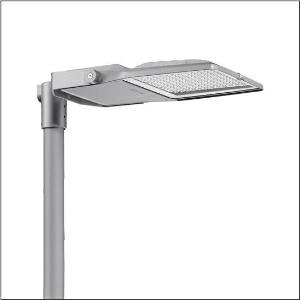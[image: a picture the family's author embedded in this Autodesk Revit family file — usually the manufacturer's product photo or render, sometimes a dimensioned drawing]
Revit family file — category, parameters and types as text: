
# Revit family: floodlight_fl_21_iq_midi___pl43_5xa7782f4a3a_c232
name_source: partatom
category: Lighting Fixtures
units: mm (PartAtom-declared; Revit-internal decimal feet)

## family parameters
Cut with Voids When Loaded = No
Host = Face
Light Source = No
Part Type = Normal
Room Calculation Point = No
Round Connector Dimension = Use Diameter
Shared = No

## types (1)
- --- (1 x LED, 38290 lm, 270.2 W, 4000K)
    Apparent Load = 270 VA
    CIE Flux Codes = 27 78 99 100 100
    Color Rendering = 70
    Color Temperature = 4000K
    Default Elevation = 1800 mm
    Description = Floodlight FL 21 iQ midi, floodlight, primary light control with lens, of PMMA, primary optical cover: protective disc, of toughened safety glass, transparent, light distribution: PL43, light emission: direct distribution, installation type: surface-mounted, lamps: LED, High Power LED, rated values: 38.290lm | 270,2W | 141,7lm/W (begin service life); end service life: 38.290lm | 286,6W; at 50% lumin. flux: 19.145lm | 117,7W | 162,7lm/W, colour temperature: 4000K, colour rendering: CRI > 70, light colour: 740, light setting 1 begin service life: 100% | 38.290lm | 270,2W | 141,7lm/W | 4.000K, light setting 1 end service life: 286,6W, further light settings possible, control: optimised constant luminous flux control (CLO 2.0), Desk-Remote (wireless, voltage-free reading and setting of iQ features in the workshop via application-optimized NFC function/RFID function), Smart-Wire, Night-Set, Temp-Guard, Auto-Match, Street-Remote, pre-setting: linear dimming characteristic, with terminal, 6-pole, mains connection: 220..240V, AC, 50/60Hz, luminaire housing, of diecast aluminium, powder-coated, SITECO metallic grey (DB 702S), corrosivity category C5 mid according to DIN EN ISO 12944suitable for swimming poolschlorine-resistant, sealing non-destructively replaceable, please order mast flange separately, mast bracket, of steel, galvanised, powder-coated, SITECO metallic grey (DB 702S), protection rating (complete): IP66, insulation class (complete): insulation class II (safety insulation), certification: CE, ENEC, VDE, protection symbol: D, impact resistance: IK08, permissible operating ambient temperature: -40..+40°C, permissible operating ambient temperature for outdoor applications: -40..+50°C, standard: DIN EN 12944, LABS conformity tested according to VDMA 24364:2018-05, packaging unit: 1 piece

Light Distribution: PL43
    Height = 76 mm
    Lamp = 1 x LED
    Lamp Light Flux = 38290 lm
    Lamp Power = 270.2 W
    Lamp count = 1
    Length = 657 mm
    Luminous efficacy = 142 lm/W
    Manufacturer = Siteco
    ModVariant = No
    Model = 5XA7782F4A3A
    Mounting Place = Pole
    Mounting Type = Pole annexe
    Number of Poles = 1
    OnlyDefault = Yes
    Power Factor = 1
    Product Name = Floodlight FL 21 iQ midi | PL43
    Product group = floodlight | pylon annexe
    ProductGroupID = 6201
    Protection Class = Protection class II
    Protection Degree = IP 66
    RLX_Detail_Level = 1
    RLX_Emergency_Light_Flux = 0 lm
    RLX_Emergency_Type = 0
    RLX_Emergency_Type_DB = No
    RlxData = <blob elided: 153573 chars, md5=3355b991>
    Socket = socket
    Standby Power = 0 W
    System Light Flux = 38290 lm
    System Power = 270 W
    Type Comments = factory setting: luminous flux: 100 % | dim-lin: 254 | 620 mA
    Type Image = l_1007123.jpg
    URL = http://relux.com
    VarID = @adj_106085
    Voltage = 0 V
    Weight = 0.00 kg
    Width = 442 mm

## geometry (parser evidence)
native form markers: Blend x4, Sweep x14
no freeform markers — native parametric forms only
